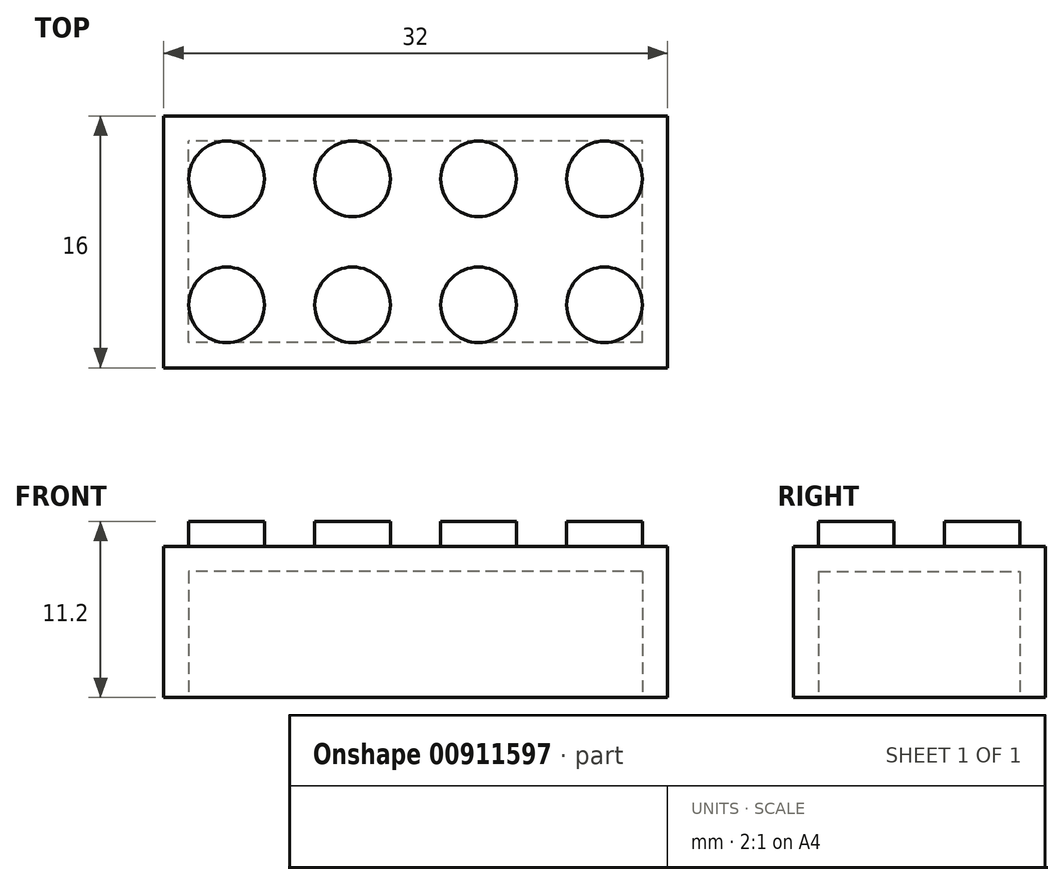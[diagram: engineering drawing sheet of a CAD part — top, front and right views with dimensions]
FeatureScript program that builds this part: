
annotation { "Feature Type Name" : "Feature", "Feature Type Description" : "" }
export const myFeature = defineFeature(function(context is Context, id is Id, definition is map)
    precondition{}
    {
        {
            var Q0;
            Q0=qCreatedBy(makeId("Top.planeOp"),FACE);
            var sketch = newSketch(context, id + "F0", { "sketchPlane" : qUnion([Q0])});
            skLineSegment(sketch, "E0.bottom", {"start": v(16, 8) * mm, "end": v(-16, 8) * mm});
            skLineSegment(sketch, "E0.top", {"start": v(16, -8) * mm, "end": v(-16, -8) * mm});
            skLineSegment(sketch, "E0.left", {"start": v(16, 8) * mm, "end": v(16, -8) * mm});
            skLineSegment(sketch, "E0.right", {"start": v(-16, 8) * mm, "end": v(-16, -8) * mm});
            skPoint(sketch, "E0.middle", {"position": v(0, 0) * mm});
            skSolve(sketch);
        }
        {
            var Q0;
            Q0=makeQuery(id+"F0.imprint","IMPRINT",FACE,{"disambiguationData":[TD([[makeQuery(id+"F0.imprint","IMPRINT",EDGE,{"derivedFrom":sQuery(id+"F0.wireOp",EDGE,"E0.bottom")}),1.0]])]});
            extrude(context, id + "F1", {"entities" : qUnion([Q0]), "depth" : 9.6 * mm, "offsetDistance" : 25 * mm});
        }
        {
            var Q0;
            Q0=makeQuery(id+"F1.opExtrude","CAP_FACE",FACE,{"disambiguationData":[OSD([sQuery(id+"F0.wireOp",EDGE,"E0.bottom"),sQuery(id+"F0.wireOp",EDGE,"E0.top"),sQuery(id+"F0.wireOp",EDGE,"E0.left"),sQuery(id+"F0.wireOp",EDGE,"E0.right")])],"isStart":true});
            var sketch = newSketch(context, id + "F2", { "sketchPlane" : qUnion([Q0])});
            skLineSegment(sketch, "E1.bottom", {"start": v(14.4, 6.4) * mm, "end": v(-14.4, 6.4) * mm});
            skLineSegment(sketch, "E1.top", {"start": v(14.4, -6.4) * mm, "end": v(-14.4, -6.4) * mm});
            skLineSegment(sketch, "E1.left", {"start": v(14.4, 6.4) * mm, "end": v(14.4, -6.4) * mm});
            skLineSegment(sketch, "E1.right", {"start": v(-14.4, 6.4) * mm, "end": v(-14.4, -6.4) * mm});
            skPoint(sketch, "E1.middle", {"position": v(0, 0) * mm});
            skSolve(sketch);
        }
        {
            var Q0;
            Q0=makeQuery(id+"F2.imprint","IMPRINT",FACE,{"disambiguationData":[TD([[makeQuery(id+"F2.imprint","IMPRINT",EDGE,{"derivedFrom":sQuery(id+"F2.wireOp",EDGE,"E1.bottom")}),1.0]])]});
            extrude(context, id + "F3", {"entities" : qUnion([Q0]), "operationType" : NewBodyOperationType.REMOVE, "oppositeDirection" : true, "depth" : 8 * mm, "offsetDistance" : 25 * mm});
        }
        {
            var Q0;
            Q0=makeQuery(id+"F1.opExtrude","CAP_FACE",FACE,{"disambiguationData":[OSD([sQuery(id+"F0.wireOp",EDGE,"E0.bottom"),sQuery(id+"F0.wireOp",EDGE,"E0.top"),sQuery(id+"F0.wireOp",EDGE,"E0.left"),sQuery(id+"F0.wireOp",EDGE,"E0.right")])],"isStart":false});
            var sketch = newSketch(context, id + "F4", { "sketchPlane" : qUnion([Q0])});
            skCircle(sketch, "E2", {"center": v(-12, 4) * mm, "radius": 2.4 * mm});
            skCircle(sketch, "E3", {"center": v(-4, 4) * mm, "radius": 2.4 * mm});
            skCircle(sketch, "E4", {"center": v(4, 4) * mm, "radius": 2.4 * mm});
            skCircle(sketch, "E5", {"center": v(12, 4) * mm, "radius": 2.4 * mm});
            skCircle(sketch, "E6", {"center": v(12, -4) * mm, "radius": 2.4 * mm});
            skCircle(sketch, "E7", {"center": v(4, -4) * mm, "radius": 2.4 * mm});
            skCircle(sketch, "E8", {"center": v(-4, -4) * mm, "radius": 2.4 * mm});
            skCircle(sketch, "E9", {"center": v(-12, -4) * mm, "radius": 2.4 * mm});
            skLineSegment(sketch, "E10", {"start": v(-12, 4) * mm, "end": v(12, 4) * mm, "construction": true});
            skSolve(sketch);
        }
        {
            var Q0;
            Q0=makeQuery(id+"F4.imprint","IMPRINT",FACE,{"disambiguationData":[TD([[makeQuery(id+"F4.imprint","IMPRINT",EDGE,{"derivedFrom":sQuery(id+"F4.wireOp",EDGE,"E2")}),1.0]])]});
            var Q1;
            Q1=makeQuery(id+"F4.imprint","IMPRINT",FACE,{"disambiguationData":[TD([[makeQuery(id+"F4.imprint","IMPRINT",EDGE,{"derivedFrom":sQuery(id+"F4.wireOp",EDGE,"E3")}),1.0]])]});
            var Q2;
            Q2=makeQuery(id+"F4.imprint","IMPRINT",FACE,{"disambiguationData":[TD([[makeQuery(id+"F4.imprint","IMPRINT",EDGE,{"derivedFrom":sQuery(id+"F4.wireOp",EDGE,"E4")}),1.0]])]});
            var Q3;
            Q3=makeQuery(id+"F4.imprint","IMPRINT",FACE,{"disambiguationData":[TD([[makeQuery(id+"F4.imprint","IMPRINT",EDGE,{"derivedFrom":sQuery(id+"F4.wireOp",EDGE,"E5")}),1.0]])]});
            var Q4;
            Q4=makeQuery(id+"F4.imprint","IMPRINT",FACE,{"disambiguationData":[TD([[makeQuery(id+"F4.imprint","IMPRINT",EDGE,{"derivedFrom":sQuery(id+"F4.wireOp",EDGE,"E9")}),1.0]])]});
            var Q5;
            Q5=makeQuery(id+"F4.imprint","IMPRINT",FACE,{"disambiguationData":[TD([[makeQuery(id+"F4.imprint","IMPRINT",EDGE,{"derivedFrom":sQuery(id+"F4.wireOp",EDGE,"E8")}),1.0]])]});
            var Q6;
            Q6=makeQuery(id+"F4.imprint","IMPRINT",FACE,{"disambiguationData":[TD([[makeQuery(id+"F4.imprint","IMPRINT",EDGE,{"derivedFrom":sQuery(id+"F4.wireOp",EDGE,"E7")}),1.0]])]});
            var Q7;
            Q7=makeQuery(id+"F4.imprint","IMPRINT",FACE,{"disambiguationData":[TD([[makeQuery(id+"F4.imprint","IMPRINT",EDGE,{"derivedFrom":sQuery(id+"F4.wireOp",EDGE,"E6")}),1.0]])]});
            extrude(context, id + "F5", {"entities" : qUnion([Q0, Q1, Q2, Q3, Q4, Q5, Q6, Q7]), "operationType" : NewBodyOperationType.ADD, "depth" : 1.6 * mm, "offsetDistance" : 25 * mm});
        }
    });
